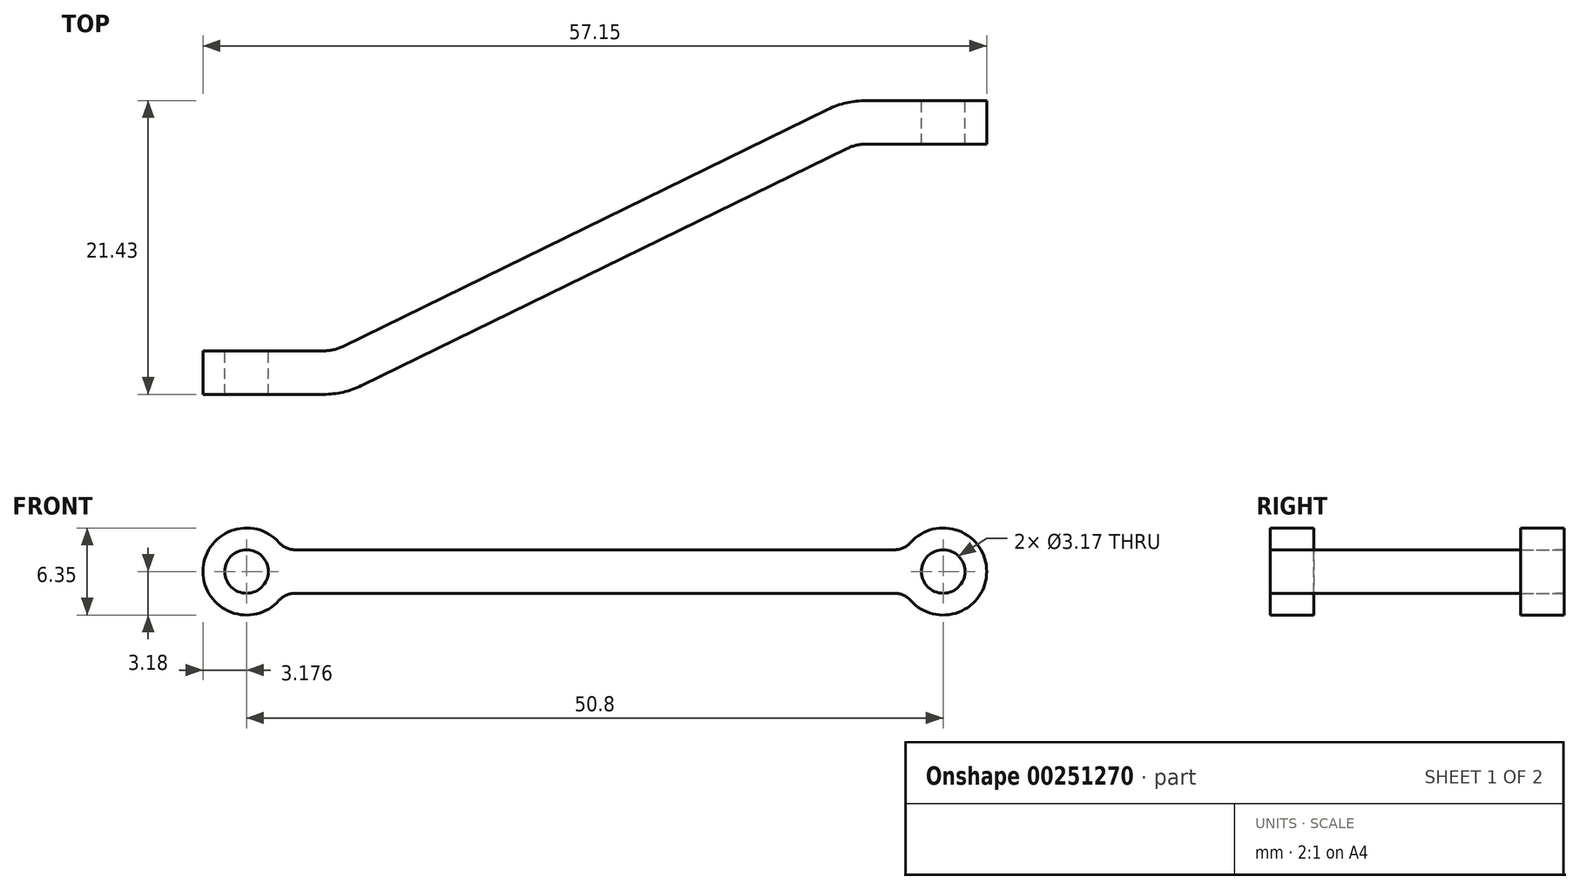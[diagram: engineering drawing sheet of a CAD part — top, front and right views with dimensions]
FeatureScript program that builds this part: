
annotation { "Feature Type Name" : "Feature", "Feature Type Description" : "" }
export const myFeature = defineFeature(function(context is Context, id is Id, definition is map)
    precondition{}
    {
        {
            var Q0;
            Q0=qCreatedBy(makeId("Front.planeOp"),FACE);
            var sketch = newSketch(context, id + "F0", { "sketchPlane" : qUnion([Q0])});
            skLineSegment(sketch, "E0.bottom", {"start": v(5.52, 35.46) * mm, "end": v(62.67, 35.46) * mm});
            skLineSegment(sketch, "E0.top", {"start": v(5.52, 29.11) * mm, "end": v(62.67, 29.11) * mm});
            skLineSegment(sketch, "E0.left", {"start": v(5.52, 35.46) * mm, "end": v(5.52, 29.11) * mm});
            skLineSegment(sketch, "E0.right", {"start": v(62.67, 35.46) * mm, "end": v(62.67, 29.11) * mm});
            skCircle(sketch, "E1", {"center": v(8.7, 32.29) * mm, "radius": 1.59 * mm});
            skCircle(sketch, "E2", {"center": v(59.5, 32.29) * mm, "radius": 1.59 * mm});
            skCircle(sketch, "E3", {"center": v(8.7, 32.29) * mm, "radius": 3.18 * mm});
            skCircle(sketch, "E4", {"center": v(59.5, 32.29) * mm, "radius": 3.18 * mm});
            skLineSegment(sketch, "E5", {"start": v(11.45, 33.88) * mm, "end": v(56.75, 33.88) * mm});
            skLineSegment(sketch, "E6", {"start": v(11.45, 30.7) * mm, "end": v(56.75, 30.7) * mm});
            skArc(sketch, "E7", {"start": v(11.06, 34.4) * mm, "mid": v(11.6, 34.02) * mm, "end": v(12.25, 33.88) * mm});
            skArc(sketch, "E8", {"start": v(12.25, 30.7) * mm, "mid": v(11.6, 30.56) * mm, "end": v(11.06, 30.17) * mm});
            skArc(sketch, "E9", {"start": v(55.95, 33.88) * mm, "mid": v(56.6, 34.02) * mm, "end": v(57.13, 34.4) * mm});
            skArc(sketch, "E10", {"start": v(57.13, 30.17) * mm, "mid": v(56.6, 30.56) * mm, "end": v(55.95, 30.7) * mm});
            skSolve(sketch);
        }
        {
            var Q0;
            Q0=makeQuery(id+"F0.imprint","IMPRINT",FACE,{"disambiguationData":[TD([[makeQuery(id+"F0.imprint","IMPRINT",EDGE,{"derivedFrom":sQuery(id+"F0.wireOp",EDGE,"E2")}),-1.0]])]});
            var Q1;
            {var subQ0=sQuery(id+"F0.wireOp",EDGE,"E5");var subQ3=sQuery(id+"F0.wireOp",EDGE,"E3");var subQ4=makeQuery(id+"F0.imprint","INTERSECT",VERTEX,{"derivedFrom":[subQ3,subQ0]});Q1=makeQuery(id+"F0.imprint","IMPRINT",FACE,{"disambiguationData":[TD([[makeQuery(id+"F0.imprint","IMPRINT",EDGE,{"disambiguationData":[TD([[subQ4,1.0]])],"derivedFrom":subQ3}),-1.0]])]});}
            var Q2;
            Q2=makeQuery(id+"F0.imprint","IMPRINT",FACE,{"disambiguationData":[TD([[makeQuery(id+"F0.imprint","IMPRINT",EDGE,{"derivedFrom":sQuery(id+"F0.wireOp",EDGE,"E1")}),-1.0]])]});
            var Q3;
            {var subQ3=sQuery(id+"F0.wireOp",EDGE,"E7");Q3=makeQuery(id+"F0.imprint","IMPRINT",FACE,{"disambiguationData":[TD([[makeQuery(id+"F0.imprint","IMPRINT",EDGE,{"derivedFrom":subQ3}),-1.0]])]});}
            var Q4;
            {var subQ3=sQuery(id+"F0.wireOp",EDGE,"E8");Q4=makeQuery(id+"F0.imprint","IMPRINT",FACE,{"disambiguationData":[TD([[makeQuery(id+"F0.imprint","IMPRINT",EDGE,{"derivedFrom":subQ3}),-1.0]])]});}
            var Q5;
            {var subQ3=sQuery(id+"F0.wireOp",EDGE,"E9");Q5=makeQuery(id+"F0.imprint","IMPRINT",FACE,{"disambiguationData":[TD([[makeQuery(id+"F0.imprint","IMPRINT",EDGE,{"derivedFrom":subQ3}),-1.0]])]});}
            var Q6;
            {var subQ3=sQuery(id+"F0.wireOp",EDGE,"E10");Q6=makeQuery(id+"F0.imprint","IMPRINT",FACE,{"disambiguationData":[TD([[makeQuery(id+"F0.imprint","IMPRINT",EDGE,{"derivedFrom":subQ3}),-1.0]])]});}
            extrude(context, id + "F1", {"entities" : qUnion([Q0, Q1, Q2, Q3, Q4, Q5, Q6]), "depth" : 21.43 * mm});
        }
        {
            var Q0;
            Q0=makeQuery(id+"F1.opExtrude","SWEPT_FACE",FACE,{"disambiguationData":[OSD([sQuery(id+"F0.wireOp",EDGE,"E5")])]});
            cPlane(context, id + "F2", {"entities" : qUnion([Q0]), "cplaneType" : CPlaneType.OFFSET, "offset" : 3.17 * mm, "width" : 152.4 * mm, "height" : 152.4 * mm});
        }
        {
            var Q0;
            Q0=qCreatedBy(id+"F2.planeOp",FACE);
            var sketch = newSketch(context, id + "F3", { "sketchPlane" : qUnion([Q0])});
            skLineSegment(sketch, "E11.0.0", {"start": v(55.95, 0) * mm, "end": v(12.25, 0) * mm});
            skLineSegment(sketch, "E11.0.1", {"start": v(12.25, 0) * mm, "end": v(12.25, -21.43) * mm});
            skLineSegment(sketch, "E11.0.2", {"start": v(12.25, -21.43) * mm, "end": v(55.95, -21.43) * mm});
            skLineSegment(sketch, "E11.0.3", {"start": v(55.95, -21.43) * mm, "end": v(55.95, 0) * mm});
            skLineSegment(sketch, "E12", {"start": v(5.52, -21.43) * mm, "end": v(5.52, 0) * mm});
            skLineSegment(sketch, "E13", {"start": v(62.67, 0) * mm, "end": v(62.67, -21.43) * mm});
            skLineSegment(sketch, "E14.0.0", {"start": v(57.13, 0) * mm, "end": v(55.95, 0) * mm});
            skLineSegment(sketch, "E14.0.1", {"start": v(55.95, 0) * mm, "end": v(55.95, -21.43) * mm});
            skLineSegment(sketch, "E14.0.2", {"start": v(55.95, -21.43) * mm, "end": v(57.13, -21.43) * mm});
            skLineSegment(sketch, "E14.0.3", {"start": v(57.13, -21.43) * mm, "end": v(57.13, 0) * mm});
            skLineSegment(sketch, "E15.0.0", {"start": v(12.25, 0) * mm, "end": v(11.06, 0) * mm});
            skLineSegment(sketch, "E15.0.1", {"start": v(11.06, 0) * mm, "end": v(11.06, -21.43) * mm});
            skLineSegment(sketch, "E15.0.2", {"start": v(11.06, -21.43) * mm, "end": v(12.25, -21.43) * mm});
            skLineSegment(sketch, "E15.0.3", {"start": v(12.25, -21.43) * mm, "end": v(12.25, 0) * mm});
            skLineSegment(sketch, "E16", {"start": v(62.67, -3.18) * mm, "end": v(53.15, -3.18) * mm});
            skLineSegment(sketch, "E17", {"start": v(53.15, -3.18) * mm, "end": v(15.78, -21.43) * mm});
            skLineSegment(sketch, "E18", {"start": v(5.52, -18.26) * mm, "end": v(15.05, -18.26) * mm});
            skLineSegment(sketch, "E19", {"start": v(15.05, -18.26) * mm, "end": v(52.41, 0) * mm});
            skArc(sketch, "E20", {"start": v(53.88, -3.18) * mm, "mid": v(53.16, -3.26) * mm, "end": v(52.49, -3.5) * mm});
            skArc(sketch, "E21", {"start": v(53.88, 0) * mm, "mid": v(52.45, -0.16) * mm, "end": v(51.1, -0.64) * mm});
            skArc(sketch, "E22", {"start": v(14.31, -18.26) * mm, "mid": v(15.03, -18.17) * mm, "end": v(15.7, -17.93) * mm});
            skArc(sketch, "E23", {"start": v(14.31, -21.43) * mm, "mid": v(15.74, -21.27) * mm, "end": v(17.1, -20.79) * mm});
            skLineSegment(sketch, "E24", {"start": v(5.52, -21.43) * mm, "end": v(11.06, -21.43) * mm});
            skLineSegment(sketch, "E25", {"start": v(57.13, 0) * mm, "end": v(62.67, 0) * mm});
            skLineSegment(sketch, "E26", {"start": v(57.13, -21.43) * mm, "end": v(62.67, -21.43) * mm});
            skLineSegment(sketch, "E27", {"start": v(11.06, 0) * mm, "end": v(5.52, 0) * mm});
            skSolve(sketch);
        }
        {
            var Q0;
            {var subQ3=sQuery(id+"F3.wireOp",EDGE,"E21");Q0=makeQuery(id+"F3.imprint","IMPRINT",FACE,{"disambiguationData":[TD([[makeQuery(id+"F3.imprint","IMPRINT",EDGE,{"derivedFrom":subQ3}),-1.0]])]});}
            var Q1;
            {var subQ0=sQuery(id+"F3.wireOp",EDGE,"E26");Q1=makeQuery(id+"F3.imprint","IMPRINT",FACE,{"disambiguationData":[TD([[makeQuery(id+"F3.imprint","IMPRINT",EDGE,{"derivedFrom":subQ0}),1.0]])]});}
            var Q2;
            {var subQ0=sQuery(id+"F3.wireOp",EDGE,"E14.0.2");Q2=makeQuery(id+"F3.imprint","IMPRINT",FACE,{"disambiguationData":[TD([[makeQuery(id+"F3.imprint","IMPRINT",EDGE,{"derivedFrom":subQ0}),1.0]])]});}
            var Q3;
            {var subQ0=sQuery(id+"F3.wireOp",EDGE,"E15.0.0");Q3=makeQuery(id+"F3.imprint","IMPRINT",FACE,{"disambiguationData":[TD([[makeQuery(id+"F3.imprint","IMPRINT",EDGE,{"derivedFrom":subQ0}),1.0]])]});}
            var Q4;
            {var subQ2=sQuery(id+"F3.wireOp",EDGE,"E22");Q4=makeQuery(id+"F3.imprint","IMPRINT",FACE,{"disambiguationData":[TD([[makeQuery(id+"F3.imprint","IMPRINT",EDGE,{"derivedFrom":subQ2}),1.0]])]});}
            var Q5;
            {var subQ0=sQuery(id+"F3.wireOp",EDGE,"E20");Q5=makeQuery(id+"F3.imprint","IMPRINT",FACE,{"disambiguationData":[TD([[makeQuery(id+"F3.imprint","IMPRINT",EDGE,{"derivedFrom":subQ0}),1.0]])]});}
            var Q6;
            {var subQ0=sQuery(id+"F3.wireOp",EDGE,"E27");Q6=makeQuery(id+"F3.imprint","IMPRINT",FACE,{"disambiguationData":[TD([[makeQuery(id+"F3.imprint","IMPRINT",EDGE,{"derivedFrom":subQ0}),1.0]])]});}
            var Q7;
            {var subQ3=sQuery(id+"F3.wireOp",EDGE,"E23");Q7=makeQuery(id+"F3.imprint","IMPRINT",FACE,{"disambiguationData":[TD([[makeQuery(id+"F3.imprint","IMPRINT",EDGE,{"derivedFrom":subQ3}),-1.0]])]});}
            extrude(context, id + "F4", {"entities" : qUnion([Q0, Q1, Q2, Q3, Q4, Q5, Q6, Q7]), "operationType" : NewBodyOperationType.REMOVE, "oppositeDirection" : true, "depth" : 25.4 * mm});
        }
    });
